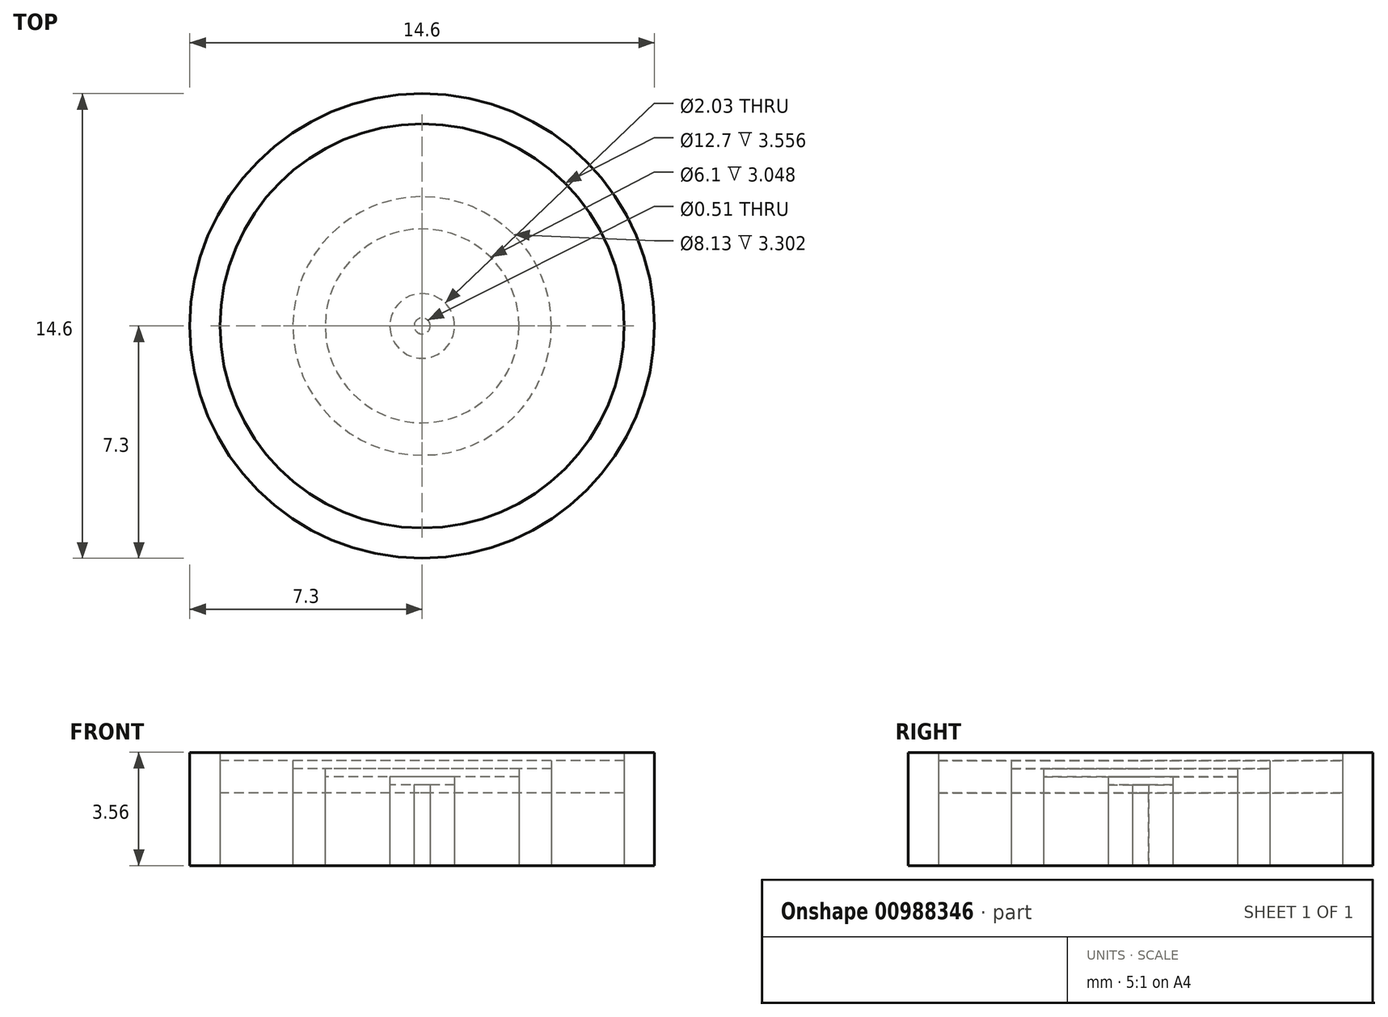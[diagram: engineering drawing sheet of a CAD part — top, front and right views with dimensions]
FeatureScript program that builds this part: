
annotation { "Feature Type Name" : "Feature", "Feature Type Description" : "" }
export const myFeature = defineFeature(function(context is Context, id is Id, definition is map)
    precondition{}
    {
        {
            var Q0;
            Q0=qCreatedBy(makeId("Top.planeOp"),FACE);
            var sketch = newSketch(context, id + "F0", { "sketchPlane" : qUnion([Q0])});
            skCircle(sketch, "E0", {"center": v(0, 0) * mm, "radius": 7.3 * mm});
            skSolve(sketch);
        }
        {
            var Q0;
            Q0=makeQuery(id+"F0.imprint","IMPRINT",FACE,{"disambiguationData":[TD([[makeQuery(id+"F0.imprint","IMPRINT",EDGE,{"derivedFrom":sQuery(id+"F0.wireOp",EDGE,"E0")}),1.0]])]});
            var sketch = newSketch(context, id + "F1", { "sketchPlane" : qUnion([Q0])});
            skCircle(sketch, "E1", {"center": v(0, 0) * mm, "radius": 6.35 * mm});
            skSolve(sketch);
        }
        {
            var Q0;
            Q0=makeQuery(id+"F1.imprint","IMPRINT",FACE,{"disambiguationData":[TD([[makeQuery(id+"F1.imprint","IMPRINT",EDGE,{"derivedFrom":sQuery(id+"F1.wireOp",EDGE,"E1")}),-1.0]])]});
            var Q1;
            Q1=sQuery(id+"F0.wireOp",EDGE,"E0");
            extrude(context, id + "F2", {"entities" : qUnion([Q0]), "surfaceEntities" : qUnion([Q1]), "depth" : 3.56 * mm, "offsetDistance" : 25.4 * mm});
        }
        {
            var Q0;
            Q0=qCreatedBy(makeId("Top.planeOp"),FACE);
            var sketch = newSketch(context, id + "F3", { "sketchPlane" : qUnion([Q0])});
            skCircle(sketch, "E2", {"center": v(0, 0) * mm, "radius": 6.35 * mm});
            skSolve(sketch);
        }
        {
            var Q0;
            Q0=makeQuery(id+"F3.imprint","IMPRINT",FACE,{"disambiguationData":[TD([[makeQuery(id+"F3.imprint","IMPRINT",EDGE,{"derivedFrom":sQuery(id+"F3.wireOp",EDGE,"E2")}),1.0]])]});
            var sketch = newSketch(context, id + "F4", { "sketchPlane" : qUnion([Q0])});
            skCircle(sketch, "E3", {"center": v(0, 0) * mm, "radius": 4.06 * mm});
            skSolve(sketch);
        }
        {
            var Q0;
            Q0=makeQuery(id+"F4.imprint","IMPRINT",FACE,{"disambiguationData":[TD([[makeQuery(id+"F4.imprint","IMPRINT",EDGE,{"derivedFrom":sQuery(id+"F4.wireOp",EDGE,"E3")}),-1.0]])]});
            extrude(context, id + "F5", {"entities" : qUnion([Q0]), "depth" : 3.3 * mm, "offsetDistance" : 25.4 * mm});
        }
        {
            var Q0;
            Q0=qCreatedBy(makeId("Top.planeOp"),FACE);
            var sketch = newSketch(context, id + "F6", { "sketchPlane" : qUnion([Q0])});
            skCircle(sketch, "E4", {"center": v(0, 0) * mm, "radius": 4.06 * mm});
            skSolve(sketch);
        }
        {
            var Q0;
            Q0=makeQuery(id+"F6.imprint","IMPRINT",FACE,{"disambiguationData":[TD([[makeQuery(id+"F6.imprint","IMPRINT",EDGE,{"derivedFrom":sQuery(id+"F6.wireOp",EDGE,"E4")}),1.0]])]});
            var sketch = newSketch(context, id + "F7", { "sketchPlane" : qUnion([Q0])});
            skCircle(sketch, "E5", {"center": v(0, 0) * mm, "radius": 3.05 * mm});
            skSolve(sketch);
        }
        {
            var Q0;
            Q0=makeQuery(id+"F7.imprint","IMPRINT",FACE,{"disambiguationData":[TD([[makeQuery(id+"F7.imprint","IMPRINT",EDGE,{"derivedFrom":sQuery(id+"F7.wireOp",EDGE,"E5")}),-1.0]])]});
            extrude(context, id + "F8", {"entities" : qUnion([Q0]), "depth" : 3.05 * mm, "offsetDistance" : 25.4 * mm});
        }
        {
            var Q0;
            Q0=qCreatedBy(makeId("Top.planeOp"),FACE);
            var sketch = newSketch(context, id + "F9", { "sketchPlane" : qUnion([Q0])});
            skCircle(sketch, "E6", {"center": v(0, 0) * mm, "radius": 3.05 * mm});
            skSolve(sketch);
        }
        {
            var Q0;
            Q0=makeQuery(id+"F9.imprint","IMPRINT",FACE,{"disambiguationData":[TD([[makeQuery(id+"F9.imprint","IMPRINT",EDGE,{"derivedFrom":sQuery(id+"F9.wireOp",EDGE,"E6")}),1.0]])]});
            var sketch = newSketch(context, id + "F10", { "sketchPlane" : qUnion([Q0])});
            skCircle(sketch, "E7", {"center": v(0, 0) * mm, "radius": 1.02 * mm});
            skSolve(sketch);
        }
        {
            var Q0;
            Q0=makeQuery(id+"F10.imprint","IMPRINT",FACE,{"disambiguationData":[TD([[makeQuery(id+"F10.imprint","IMPRINT",EDGE,{"derivedFrom":sQuery(id+"F10.wireOp",EDGE,"E7")}),-1.0]])]});
            extrude(context, id + "F11", {"entities" : qUnion([Q0]), "depth" : 2.8 * mm, "offsetDistance" : 25.4 * mm});
        }
        {
            var Q0;
            Q0=qCreatedBy(makeId("Top.planeOp"),FACE);
            var sketch = newSketch(context, id + "F12", { "sketchPlane" : qUnion([Q0])});
            skCircle(sketch, "E8", {"center": v(0, 0) * mm, "radius": 1.02 * mm});
            skSolve(sketch);
        }
        {
            var Q0;
            Q0=makeQuery(id+"F12.imprint","IMPRINT",FACE,{"disambiguationData":[TD([[makeQuery(id+"F12.imprint","IMPRINT",EDGE,{"derivedFrom":sQuery(id+"F12.wireOp",EDGE,"E8")}),1.0]])]});
            var sketch = newSketch(context, id + "F13", { "sketchPlane" : qUnion([Q0])});
            skCircle(sketch, "E9", {"center": v(0, 0) * mm, "radius": 0.25 * mm});
            skSolve(sketch);
        }
        {
            var Q0;
            Q0=makeQuery(id+"F13.imprint","IMPRINT",FACE,{"disambiguationData":[TD([[makeQuery(id+"F13.imprint","IMPRINT",EDGE,{"derivedFrom":sQuery(id+"F13.wireOp",EDGE,"E9")}),-1.0]])]});
            extrude(context, id + "F14", {"entities" : qUnion([Q0]), "depth" : 2.54 * mm, "offsetDistance" : 25.4 * mm});
        }
        {
            var Q0;
            Q0=qCreatedBy(makeId("Top.planeOp"),FACE);
            var sketch = newSketch(context, id + "F15", { "sketchPlane" : qUnion([Q0])});
            skCircle(sketch, "E10", {"center": v(0, 0) * mm, "radius": 0.25 * mm});
            skSolve(sketch);
        }
        {
            var Q0;
            Q0=makeQuery(id+"F15.imprint","IMPRINT",FACE,{"disambiguationData":[TD([[makeQuery(id+"F15.imprint","IMPRINT",EDGE,{"derivedFrom":sQuery(id+"F15.wireOp",EDGE,"E10")}),1.0]])]});
            extrude(context, id + "F16", {"entities" : qUnion([Q0]), "depth" : 2.3 * mm, "offsetDistance" : 25.4 * mm});
        }
        {
            var Q0;
            Q0=makeQuery(id+"F16.opExtrude","CAP_FACE",FACE,{"disambiguationData":[OSD([sQuery(id+"F15.wireOp",EDGE,"E10")])],"isStart":false});
            var sketch = newSketch(context, id + "F17", { "sketchPlane" : qUnion([Q0])});
            skCircle(sketch, "E11", {"center": v(0, 0) * mm, "radius": 6.35 * mm});
            skSolve(sketch);
        }
        {
            var Q0;
            Q0 = qSketchRegion(id + "F17", true);
            extrude(context, id + "F18", {"entities" : qUnion([Q0]), "depth" : 1.27 * mm, "offsetDistance" : 25.4 * mm});
        }
    });
